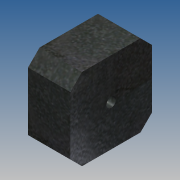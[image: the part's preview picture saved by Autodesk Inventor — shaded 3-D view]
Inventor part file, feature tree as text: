
AUTODESK INVENTOR PART (.ipt)
format: ipt  version: 2015 (Build 190159000, 159)  size: 117,248 bytes
history: native  units: mm
features: extrude x1, sketch x1
ambient origin geometry x8: Origin, YZ Plane, XZ Plane, XY Plane, X Axis, Y Axis, Z Axis, Center Point
bodies: Volumenkörper1 (feature_tree)
feature tree (2):
  extrude  "Extrusion1"  Depth=42.3mm
  sketch  "Skizze1"  dims[d0=42.3mm d1=42.3mm d2=6.0mm d3=6.0mm d4=6.0mm d5=6.0mm d6=6.0mm d7=6.0mm d8=6.0mm d9=6.0mm d10=5.0mm d11=22.0mm d12=0.0mm]
